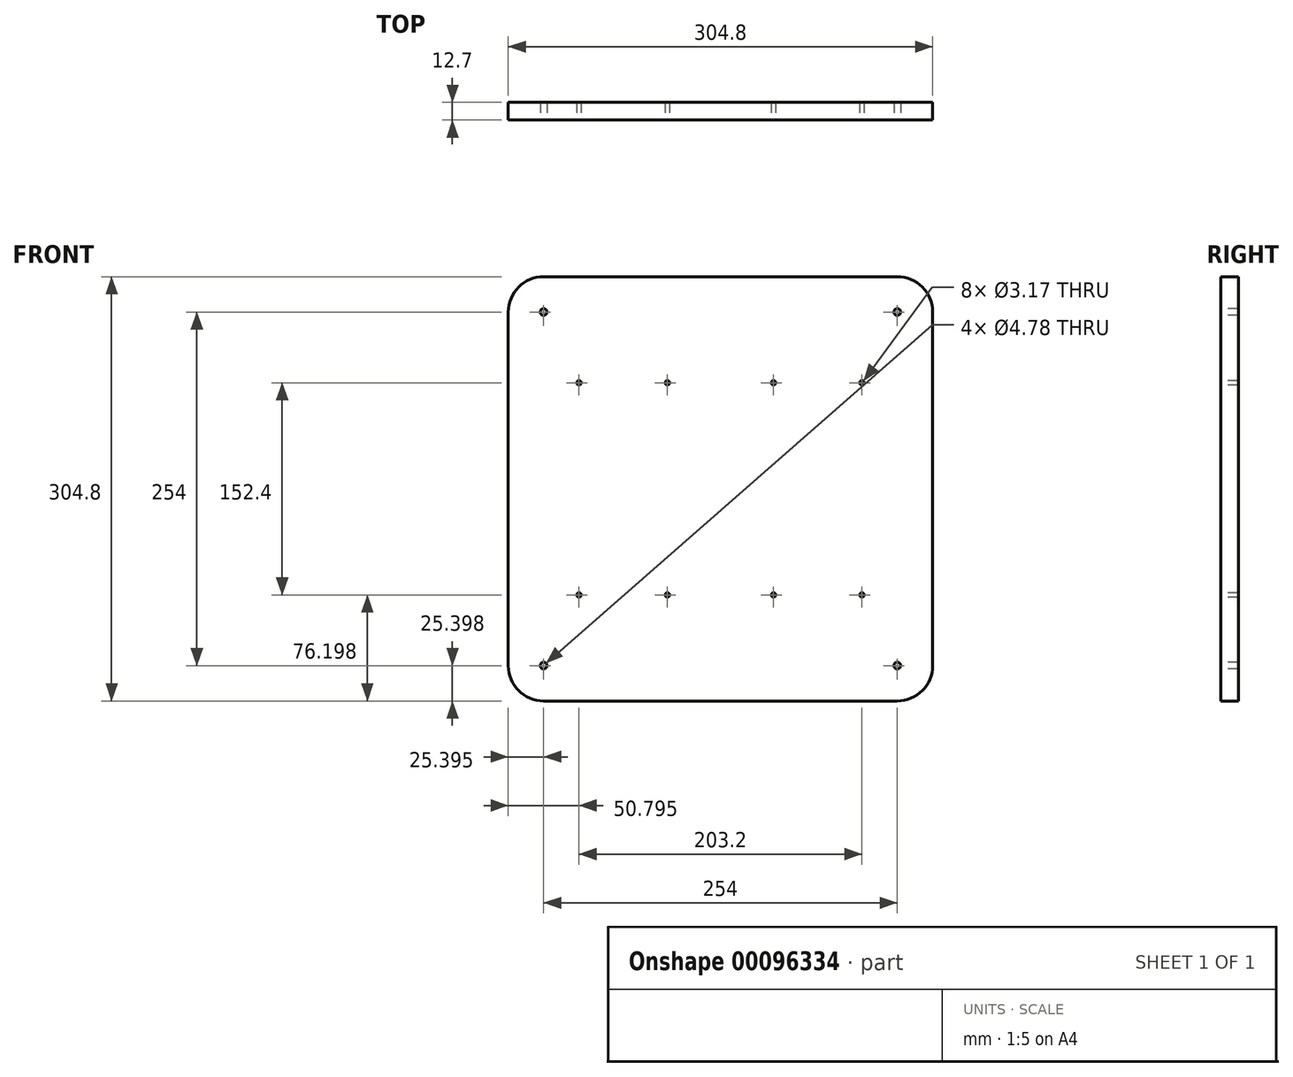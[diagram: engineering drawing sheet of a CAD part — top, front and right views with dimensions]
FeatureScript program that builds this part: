
annotation { "Feature Type Name" : "Feature", "Feature Type Description" : "" }
export const myFeature = defineFeature(function(context is Context, id is Id, definition is map)
    precondition{}
    {
        {
            var Q0;
            Q0=qCreatedBy(makeId("Front.planeOp"),FACE);
            var sketch = newSketch(context, id + "F0", { "sketchPlane" : qUnion([Q0])});
            skLineSegment(sketch, "E0.bottom", {"start": v(-198.04, 145.85) * mm, "end": v(106.76, 145.85) * mm});
            skLineSegment(sketch, "E0.top", {"start": v(-198.04, -158.95) * mm, "end": v(106.76, -158.95) * mm});
            skLineSegment(sketch, "E0.left", {"start": v(-198.04, 145.85) * mm, "end": v(-198.04, -158.95) * mm});
            skLineSegment(sketch, "E0.right", {"start": v(106.76, 145.85) * mm, "end": v(106.76, -158.95) * mm});
            skSolve(sketch);
        }
        {
            var Q0;
            Q0 = qSketchRegion(id + "F0", true);
            extrude(context, id + "F1", {"entities" : qUnion([Q0]), "depth" : 12.7 * mm});
        }
        {
            var Q0;
            Q0=makeQuery(id+"F1.opExtrude","SWEPT_EDGE",EDGE,{"disambiguationData":[OSD([sQuery(id+"F0.wireOp",EDGE,"E0.bottom"),sQuery(id+"F0.wireOp",EDGE,"E0.left")])]});
            var Q1;
            Q1=makeQuery(id+"F1.opExtrude","SWEPT_EDGE",EDGE,{"disambiguationData":[OSD([sQuery(id+"F0.wireOp",EDGE,"E0.bottom"),sQuery(id+"F0.wireOp",EDGE,"E0.right")])]});
            var Q2;
            Q2=makeQuery(id+"F1.opExtrude","SWEPT_EDGE",EDGE,{"disambiguationData":[OSD([sQuery(id+"F0.wireOp",EDGE,"E0.top"),sQuery(id+"F0.wireOp",EDGE,"E0.left")])]});
            var Q3;
            Q3=makeQuery(id+"F1.opExtrude","SWEPT_EDGE",EDGE,{"disambiguationData":[OSD([sQuery(id+"F0.wireOp",EDGE,"E0.top"),sQuery(id+"F0.wireOp",EDGE,"E0.right")])]});
            fillet(context, id + "F2", {"entities" : qUnion([Q0, Q1, Q2, Q3]), "radius" : 25.4 * mm, "tangentPropagation" : true, "allowEdgeOverflow" : false});
        }
        {
            var Q0;
            Q0=makeQuery(id+"F1.opExtrude","CAP_FACE",FACE,{"disambiguationData":[OSD([sQuery(id+"F0.wireOp",EDGE,"E0.bottom"),sQuery(id+"F0.wireOp",EDGE,"E0.top"),sQuery(id+"F0.wireOp",EDGE,"E0.left"),sQuery(id+"F0.wireOp",EDGE,"E0.right")])],"isStart":false});
            var sketch = newSketch(context, id + "F3", { "sketchPlane" : qUnion([Q0])});
            skCircle(sketch, "E1", {"center": v(-172.64, -133.55) * mm, "radius": 2.39 * mm});
            skCircle(sketch, "E2", {"center": v(81.36, -133.55) * mm, "radius": 2.39 * mm});
            skCircle(sketch, "E3.MirrorC", {"center": v(81.36, 120.45) * mm, "radius": 2.39 * mm});
            skCircle(sketch, "E4.MirrorC", {"center": v(-172.64, 120.45) * mm, "radius": 2.39 * mm});
            skSolve(sketch);
        }
        {
            var Q0;
            Q0 = qSketchRegion(id + "F3", true);
            extrude(context, id + "F4", {"entities" : qUnion([Q0]), "operationType" : NewBodyOperationType.REMOVE, "endBound" : BoundingType.THROUGH_ALL, "oppositeDirection" : true, "depth" : 25.4 * mm});
        }
        {
            var Q0;
            Q0=makeQuery(id+"F1.opExtrude","CAP_FACE",FACE,{"disambiguationData":[OSD([sQuery(id+"F0.wireOp",EDGE,"E0.bottom"),sQuery(id+"F0.wireOp",EDGE,"E0.top"),sQuery(id+"F0.wireOp",EDGE,"E0.left"),sQuery(id+"F0.wireOp",EDGE,"E0.right")])],"isStart":false});
            var sketch = newSketch(context, id + "F5", { "sketchPlane" : qUnion([Q0])});
            skCircle(sketch, "E5", {"center": v(-147.24, 69.65) * mm, "radius": 1.59 * mm});
            skCircle(sketch, "E6", {"center": v(-83.74, 69.65) * mm, "radius": 1.59 * mm});
            skCircle(sketch, "E7", {"center": v(-7.54, 69.65) * mm, "radius": 1.59 * mm});
            skCircle(sketch, "E8", {"center": v(55.96, 69.65) * mm, "radius": 1.59 * mm});
            skCircle(sketch, "E9.MirrorC", {"center": v(-147.24, -82.75) * mm, "radius": 1.59 * mm});
            skCircle(sketch, "E10.MirrorC", {"center": v(-83.74, -82.75) * mm, "radius": 1.59 * mm});
            skCircle(sketch, "E11.MirrorC", {"center": v(-7.54, -82.75) * mm, "radius": 1.59 * mm});
            skCircle(sketch, "E12.MirrorC", {"center": v(55.96, -82.75) * mm, "radius": 1.59 * mm});
            skSolve(sketch);
        }
        {
            var Q0;
            Q0 = qSketchRegion(id + "F5", true);
            extrude(context, id + "F6", {"entities" : qUnion([Q0]), "operationType" : NewBodyOperationType.REMOVE, "endBound" : BoundingType.THROUGH_ALL, "oppositeDirection" : true, "depth" : 25.4 * mm});
        }
    });
